# Revit family: Water_Heaters_HAJDU_HAJDU-STXL-750C-900C_1
name_source: partatom
category: Mechanical Equipment
units: mm (PartAtom-declared; Revit-internal decimal feet)

## family parameters
Always vertical = Yes
Classification = None
Cut with Voids When Loaded = No
Maintain Annotation Orientation = No
OmniClass Number = 23.31.29.13
OmniClass Title = Hot Water Tank Heaters
Part Type = Normal
Room Calculation Point = No
Round Connector Dimension = Use Diameter
Shared = No
Work Plane-Based = Yes

## types (2) — shared parameters
Case Material = Hajdu - Felület - Fehér
Církulációs csonk = 31.75 mm  [stored 0.104167 ft]
Default Elevation = 1219.2 mm  [stored 4 ft]
Description = A nagy teljesítményű tárolók, amelyek alkalmasak bármilyen hőtermelő eszközzel való felfűtésre, de a nagy felületű hőcserélőjüknek köszönhetően különösen célszerűek kondenzációs kazánokhoz és alacsony hőmérsékletű fűtési rendszerekhez. Nem rendelkezik különálló fűtőbetéttel de utólagosan is van lehetőség a behelyezésére, mely által használati melegvizet biztosítanak kazán vagy napkollektor nélkül is. A nagy teljesítményű, STXL típusú tartályokat kifejezetten hőszivattyús rendszerekhez ajánljuk.
Elektromos futopatron csatlakozás = 38.1 mm  [stored 0.125 ft]
Energiahatékonysági osztály = C
Hocserélo csatlakozás = 31.75 mm  [stored 0.104167 ft]
Homéro csonk = 12.7 mm  [stored 0.0416667 ft]
Manufacturer = HAJDU
Product Page URL = https://hajdurt.hu
Rádiusz = 500 mm  [stored 1.64042 ft]
URL = https://hajdurt.hu
Vízcsatlakozás = 38.1 mm  [stored 0.125 ft]
Átméro = 1000 mm  [stored 3.28084 ft]
Átméro (szigetelés nélkül) = 790 mm  [stored 2.59186 ft]
Érzékelo tokcso = 12.7 mm  [stored 0.0416667 ft]
Üzemi nyomás = 1.0 MPa

## per-type parameters (varying)
| type | Csatlakozó magassága "A" | Csatlakozó magassága "B" | Csatlakozó magassága "C" | Csatlakozó magassága "E" | Csatlakozó magassága "F" | Hocserélo felulete | Hocserélo névleges urtartalma | Hocserélo tartós teljesítmény | Magasság | Magasság (szigetelés nélkül) | Névleges urtartalom | Tárolási veszteség | Tömeg |
| STXL 750C | 1265 mm  [stored 4.15026 ft] | 1000 mm  [stored 3.28084 ft] | 1165 mm  [stored 3.82218 ft] | 1310 mm  [stored 4.2979 ft] | 1580 mm  [stored 5.18373 ft] | 6 m2 | 42 l | 180 kW | 2000 mm  [stored 6.56168 ft] | 1882 mm | 750 l | 106.7 W | 317.00 kg |
| STXL 900C | 1445 mm | 1180 mm  [stored 3.87139 ft] | 1345 mm | 1490 mm  [stored 4.88845 ft] | 1920 mm  [stored 6.29921 ft] | 7.5 m2 | 52.5 l | 225 kW | 2350 mm | 2228 mm  [stored 7.30971 ft] | 900 l | 119.6 W | 374.00 kg |

note: column(s) folded — value = type name in every type: Model

note: [stored X ft] marks values corroborated as IEEE doubles in the binary element streams (Revit-internal decimal feet)

## geometry (parser evidence)
native form markers: Sweep x4
no freeform markers — native parametric forms only
